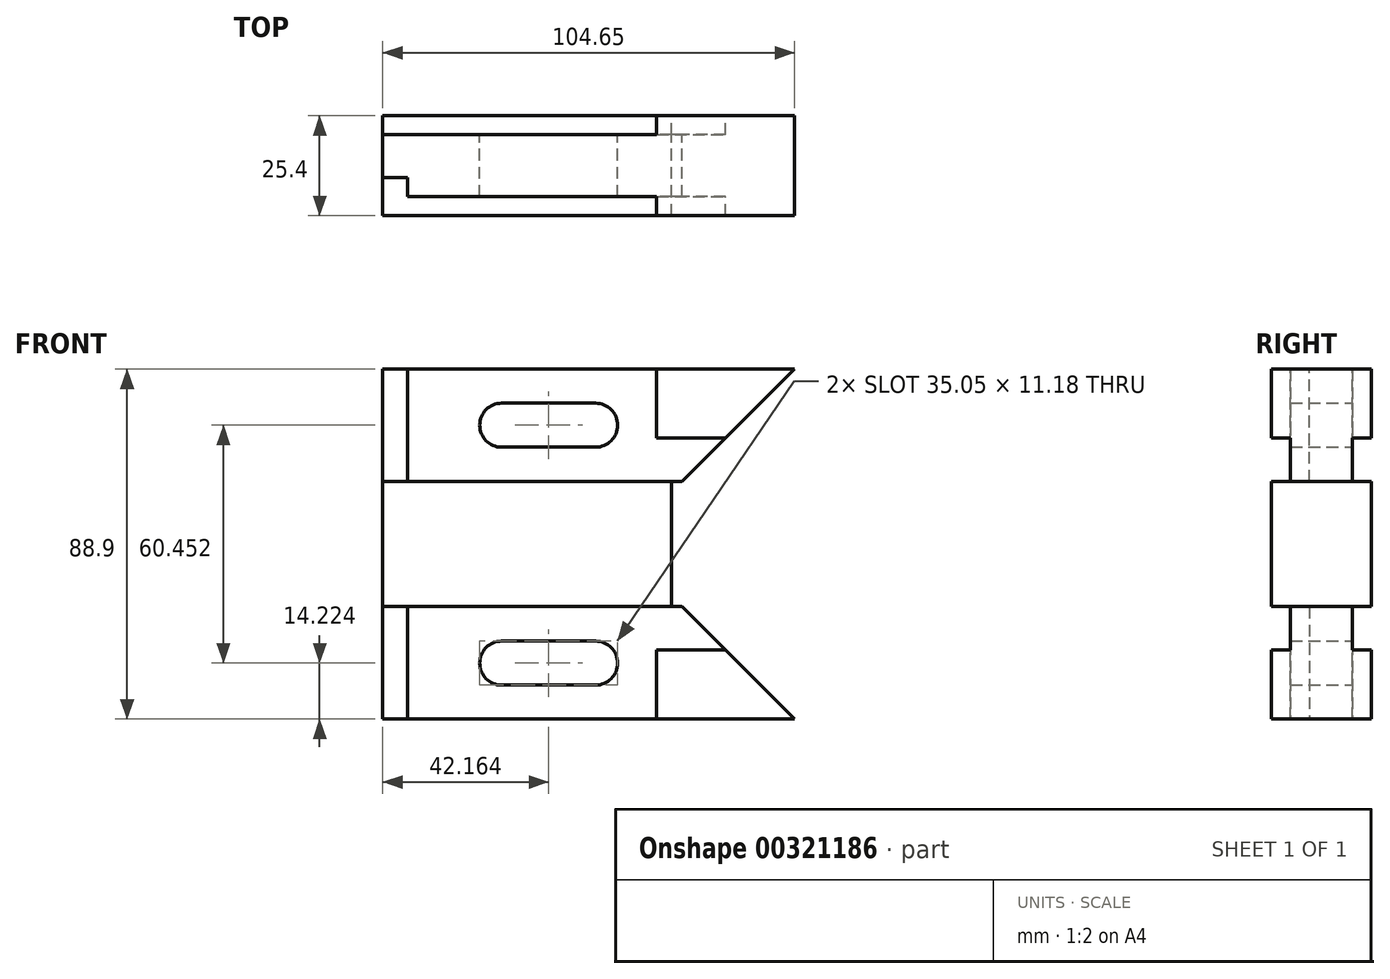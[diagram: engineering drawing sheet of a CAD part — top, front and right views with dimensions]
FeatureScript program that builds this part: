
annotation { "Feature Type Name" : "Feature", "Feature Type Description" : "" }
export const myFeature = defineFeature(function(context is Context, id is Id, definition is map)
    precondition{}
    {
        {
            var Q0;
            Q0=qCreatedBy(makeId("Front.planeOp"),FACE);
            var sketch = newSketch(context, id + "F0", { "sketchPlane" : qUnion([Q0])});
            skLineSegment(sketch, "E0", {"start": v(-81.85, 0) * mm, "end": v(77.79, 0) * mm, "construction": true});
            skLineSegment(sketch, "E1", {"start": v(0, 0) * mm, "end": v(0, 44.45) * mm});
            skLineSegment(sketch, "E2", {"start": v(0, 44.45) * mm, "end": v(104.65, 44.45) * mm});
            skLineSegment(sketch, "E3", {"start": v(104.65, 44.45) * mm, "end": v(76.07, 15.88) * mm});
            skLineSegment(sketch, "E4", {"start": v(76.07, 15.88) * mm, "end": v(0, 15.88) * mm});
            skLineSegment(sketch, "E5", {"start": v(69.6, 44.45) * mm, "end": v(69.6, 26.92) * mm});
            skLineSegment(sketch, "E6", {"start": v(69.6, 26.92) * mm, "end": v(87.12, 26.92) * mm});
            skLineSegment(sketch, "E7", {"start": v(73.4, 15.88) * mm, "end": v(73.4, 0) * mm});
            skLineSegment(sketch, "E8.bottom", {"start": v(30.23, 35.81) * mm, "end": v(54.1, 35.81) * mm});
            skLineSegment(sketch, "E8.top", {"start": v(30.23, 24.64) * mm, "end": v(54.1, 24.64) * mm});
            skArc(sketch, "E9", {"start": v(30.23, 35.81) * mm, "mid": v(24.64, 30.23) * mm, "end": v(30.23, 24.64) * mm});
            skArc(sketch, "E10", {"start": v(54.1, 24.64) * mm, "mid": v(59.69, 30.23) * mm, "end": v(54.1, 35.81) * mm});
            skPoint(sketch, "E11", {"position": v(24.64, 30.23) * mm});
            skLineSegment(sketch, "E12", {"start": v(0, 0) * mm, "end": v(73.4, 0) * mm});
            skSolve(sketch);
        }
        {
            var Q0;
            {var subQ1=sQuery(id+"F0.wireOp",EDGE,"E5");Q0=makeQuery(id+"F0.imprint","IMPRINT",FACE,{"disambiguationData":[TD([[makeQuery(id+"F0.imprint","IMPRINT",EDGE,{"derivedFrom":subQ1}),-1.0]])]});}
            extrude(context, id + "F1", {"entities" : qUnion([Q0]), "endBound" : BoundingType.SYMMETRIC, "depth" : 15.75 * mm});
        }
        {
            var Q0;
            {var subQ3=sQuery(id+"F0.wireOp",EDGE,"E5");Q0=makeQuery(id+"F0.imprint","IMPRINT",FACE,{"disambiguationData":[TD([[makeQuery(id+"F0.imprint","IMPRINT",EDGE,{"derivedFrom":subQ3}),1.0]])]});}
            extrude(context, id + "F2", {"entities" : qUnion([Q0]), "operationType" : NewBodyOperationType.ADD, "endBound" : BoundingType.SYMMETRIC, "depth" : 25.4 * mm});
        }
        {
            var Q0;
            {var subQ4=sQuery(id+"F0.wireOp",EDGE,"E7");Q0=makeQuery(id+"F0.imprint","IMPRINT",FACE,{"disambiguationData":[TD([[makeQuery(id+"F0.imprint","IMPRINT",EDGE,{"derivedFrom":subQ4}),-1.0]])]});}
            extrude(context, id + "F3", {"entities" : qUnion([Q0]), "operationType" : NewBodyOperationType.ADD, "endBound" : BoundingType.SYMMETRIC, "depth" : 25.4 * mm});
        }
        {
            var Q0;
            Q0=makeQuery(id+"F1.opExtrude","CAP_FACE",FACE,{"disambiguationData":[OSD([sQuery(id+"F0.wireOp",EDGE,"E1"),sQuery(id+"F0.wireOp",EDGE,"E2"),sQuery(id+"F0.wireOp",EDGE,"E3"),sQuery(id+"F0.wireOp",EDGE,"E4"),sQuery(id+"F0.wireOp",EDGE,"E5"),sQuery(id+"F0.wireOp",EDGE,"E6"),sQuery(id+"F0.wireOp",EDGE,"E8.bottom"),sQuery(id+"F0.wireOp",EDGE,"E8.top"),sQuery(id+"F0.wireOp",EDGE,"E9"),sQuery(id+"F0.wireOp",EDGE,"E10")])],"isStart":false});
            var sketch = newSketch(context, id + "F4", { "sketchPlane" : qUnion([Q0])});
            skLineSegment(sketch, "E13", {"start": v(0, 44.45) * mm, "end": v(0, 15.88) * mm});
            skLineSegment(sketch, "E14", {"start": v(0, 15.88) * mm, "end": v(6.35, 15.88) * mm});
            skLineSegment(sketch, "E15", {"start": v(6.35, 15.88) * mm, "end": v(6.35, 44.45) * mm});
            skLineSegment(sketch, "E16", {"start": v(6.35, 44.45) * mm, "end": v(0, 44.45) * mm});
            skSolve(sketch);
        }
        {
            var Q0;
            Q0=makeQuery(id+"F4.imprint","IMPRINT",FACE,{"disambiguationData":[TD([[makeQuery(id+"F4.imprint","IMPRINT",EDGE,{"derivedFrom":sQuery(id+"F4.wireOp",EDGE,"E13")}),-1.0]])]});
            extrude(context, id + "F5", {"entities" : qUnion([Q0]), "operationType" : NewBodyOperationType.REMOVE, "oppositeDirection" : true, "depth" : 4.83 * mm});
        }
        {
            var Q0;
            Q0=makeQuery(id+"F1.opExtrude","SWEPT_BODY",BODY,{"disambiguationData":[OSD([sQuery(id+"F0.wireOp",EDGE,"E1"),sQuery(id+"F0.wireOp",EDGE,"E2"),sQuery(id+"F0.wireOp",EDGE,"E3"),sQuery(id+"F0.wireOp",EDGE,"E4"),sQuery(id+"F0.wireOp",EDGE,"E5"),sQuery(id+"F0.wireOp",EDGE,"E6"),sQuery(id+"F0.wireOp",EDGE,"E8.bottom"),sQuery(id+"F0.wireOp",EDGE,"E8.top"),sQuery(id+"F0.wireOp",EDGE,"E9"),sQuery(id+"F0.wireOp",EDGE,"E10")])]});
            var Q1;
            Q1=qCreatedBy(makeId("Top.planeOp"),FACE);
            mirror(context, id + "F6", {"operationType" : NewBodyOperationType.ADD, "entities" : qUnion([Q0]), "mirrorPlane" : qUnion([Q1])});
        }
    });
